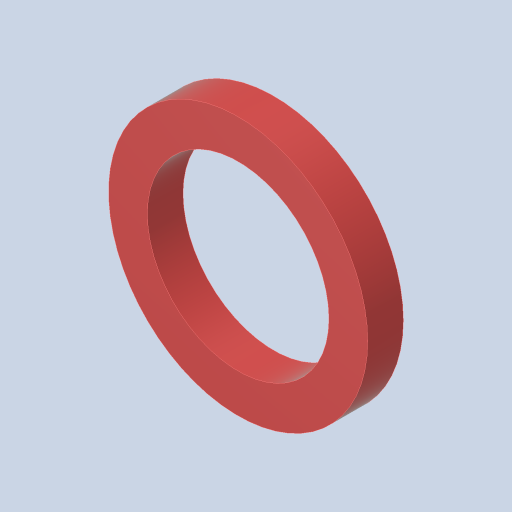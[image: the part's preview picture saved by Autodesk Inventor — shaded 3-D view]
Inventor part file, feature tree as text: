
AUTODESK INVENTOR PART (.ipt)
format: ipt  version: 2023.4 (Build 274418000, 418)  size: 116,224 bytes
history: native  units: in
note: dims shown in document units (in); Inventor stores cm internally (conversion verified against a paired STEP export)
features: extrude x1, sketch x1
ambient origin geometry x8: Origin, YZ Plane, XZ Plane, XY Plane, X Axis, Y Axis, Z Axis, Center Point
bodies: Solid1 (feature_tree)
feature tree (2):
  extrude  "Extrusion1"  Depth=0.115in
  sketch  "Sketch1"  dims[d0=0.585in d1=0.125in d2=0.115in d3=0.0in]
